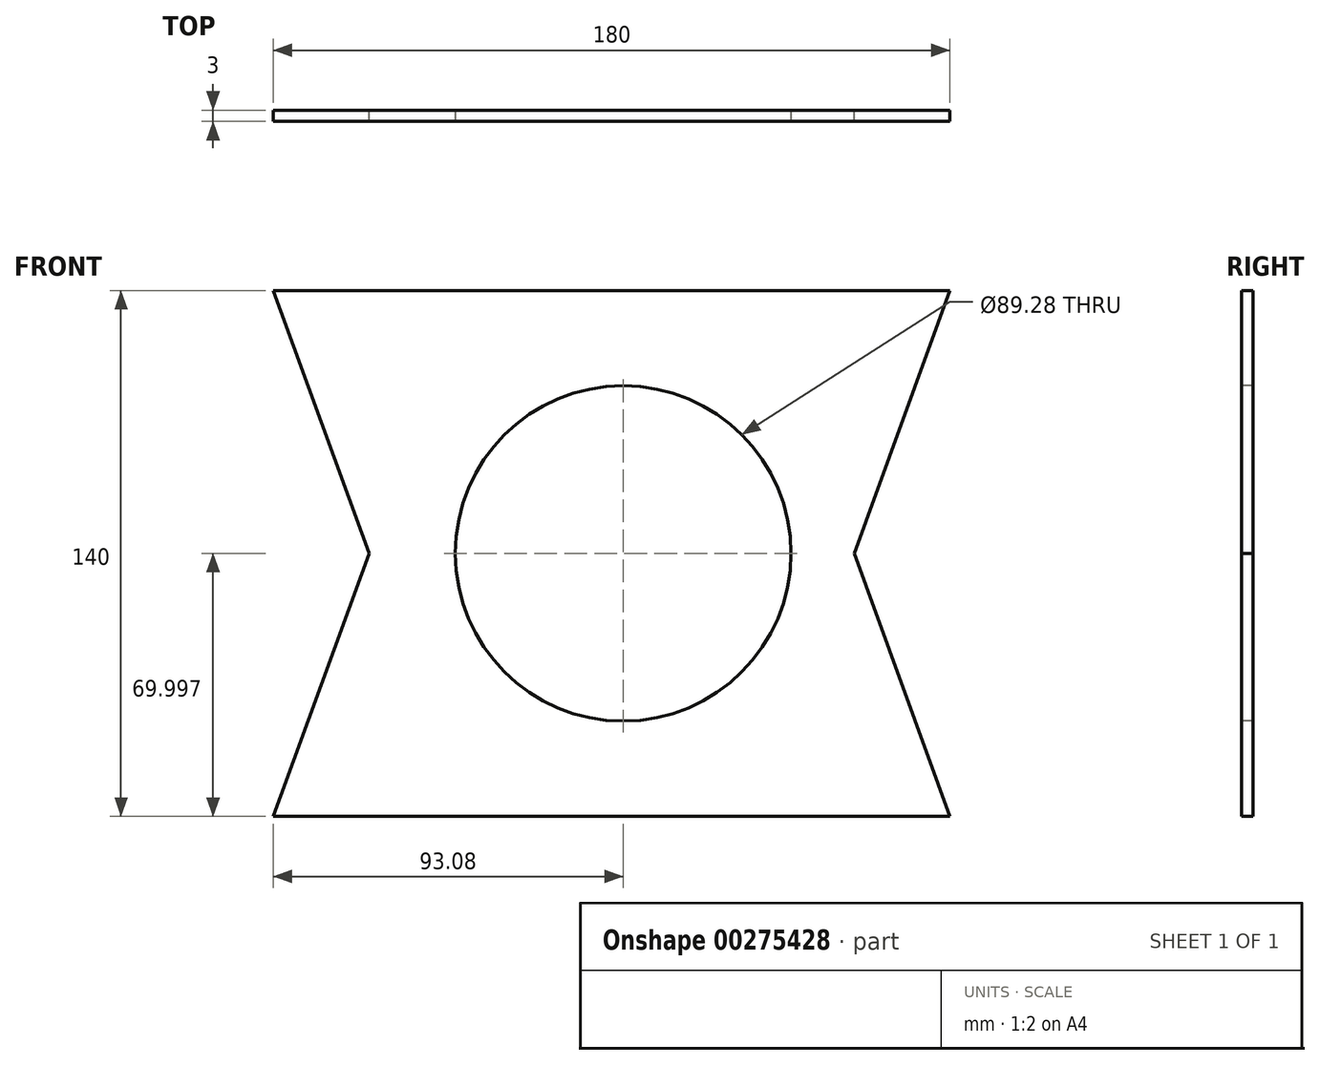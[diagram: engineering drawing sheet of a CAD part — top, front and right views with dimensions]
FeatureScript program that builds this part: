
annotation { "Feature Type Name" : "Feature", "Feature Type Description" : "" }
export const myFeature = defineFeature(function(context is Context, id is Id, definition is map)
    precondition{}
    {
        {
            var Q0;
            Q0=qCreatedBy(makeId("Front.planeOp"),FACE);
            var sketch = newSketch(context, id + "F0", { "sketchPlane" : qUnion([Q0])});
            skLineSegment(sketch, "E0.bottom", {"start": v(-93.08, 36.9) * mm, "end": v(86.92, 36.9) * mm});
            skLineSegment(sketch, "E0.top", {"start": v(-93.08, -103.1) * mm, "end": v(86.92, -103.1) * mm});
            skLineSegment(sketch, "E1", {"start": v(-93.08, 36.9) * mm, "end": v(-67.6, -33.1) * mm});
            skLineSegment(sketch, "E2", {"start": v(-67.6, -33.1) * mm, "end": v(-93.08, -103.1) * mm});
            skLineSegment(sketch, "E3", {"start": v(86.92, 36.9) * mm, "end": v(61.44, -33.1) * mm});
            skLineSegment(sketch, "E4", {"start": v(61.44, -33.1) * mm, "end": v(86.92, -103.1) * mm});
            skPoint(sketch, "E5.center.orphan", {"position": v(-3.08, -33.1) * mm});
            skSolve(sketch);
        }
        {
            var Q0;
            Q0=qSketchRegion(id+"F0",true);
            extrude(context, id + "F1", {"entities" : qUnion([Q0]), "depth" : 3 * mm});
        }
        {
            var Q0;
            Q0=makeQuery(id+"F1.opExtrude","CAP_FACE",FACE,{"disambiguationData":[OSD([sQuery(id+"F0.wireOp",EDGE,"E0.bottom"),sQuery(id+"F0.wireOp",EDGE,"E0.top"),sQuery(id+"F0.wireOp",EDGE,"E1"),sQuery(id+"F0.wireOp",EDGE,"E2"),sQuery(id+"F0.wireOp",EDGE,"E3"),sQuery(id+"F0.wireOp",EDGE,"E4")])],"isStart":false});
            var sketch = newSketch(context, id + "F2", { "sketchPlane" : qUnion([Q0])});
            skCircle(sketch, "E6", {"center": v(0, -33.1) * mm, "radius": 44.64 * mm});
            skSolve(sketch);
        }
        {
            var Q0;
            Q0 = qSketchRegion(id + "F2", true);
            extrude(context, id + "F3", {"entities" : qUnion([Q0]), "operationType" : NewBodyOperationType.REMOVE, "oppositeDirection" : true, "depth" : 135 * mm, "offsetDistance" : 25 * mm});
        }
    });
